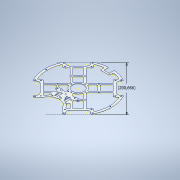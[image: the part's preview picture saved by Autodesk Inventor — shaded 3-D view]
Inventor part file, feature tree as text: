
AUTODESK INVENTOR PART (.ipt)
format: ipt  version: 2020 (Build 240168000, 168)  size: 2,045,440 bytes
history: native  units: mm
features: extrude x15, sketch x12, projected_geometry x10, fillet x2, other x1, chamfer x1
ambient origin geometry x8: Origin, YZ Plane, XZ Plane, XY Plane, X Axis, Y Axis, Z Axis, Center Point
bodies: Body1 (feature_tree)
feature tree (41):
  other  "Твердое тело1"
  extrude  "outer"  TaperAngle=45.0deg  [1 undecoded]
  extrude  "inner"  Depth=7.0mm
  sketch  "Эскиз3"
  extrude  "Выдавливание3"  Depth=20.0mm
  extrude  "Выдавливание4"  Depth=7.0mm
  extrude  "Выдавливание5"  Depth=3.2mm
  sketch  "Эскиз5"
  extrude  "Выдавливание7"  Depth=59.0mm
  extrude  "Выдавливание8"  Depth=83.0mm
  sketch  "Эскиз6"
  extrude  "Выдавливание9"  Depth=69.0mm
  extrude  "Выдавливание10"  Depth=55.0mm
  sketch  "Эскиз7"
  sketch  "Эскиз8"
  sketch  "Эскиз9"
  extrude  "Выдавливание11"  Depth=3.0mm
  extrude  "Выдавливание12"  Depth=8.0mm
  sketch  "Эскиз10"
  extrude  "Выдавливание13"  Depth=5.0mm
  extrude  "Выдавливание14"  Depth=2.0mm
  fillet  "Сопряжение1"  Radius=40.0mm
  chamfer  "Фаска1"  Distance=2.0mm
  sketch  "Эскиз11"
  extrude  "Выдавливание15"  Depth=105.0mm
  fillet  "Сопряжение2"  Radius=2.0mm
  extrude  "Выдавливание16"  Depth=2.0mm TaperAngle=0.0deg
  sketch  "Эскиз1"
  sketch  "Эскиз2"
  projected_geometry  "Спроецированная петля1"
  projected_geometry  "Спроецированная петля2"
  sketch  "Эскиз4"
  projected_geometry  "Спроецированная петля3"
  projected_geometry  "Спроецированная петля4"
  projected_geometry  "Спроецированная петля5"
  projected_geometry  "Спроецированная петля6"
  projected_geometry  "Спроецированная петля7"
  projected_geometry  "Спроецированная петля8"
  projected_geometry  "Спроецированная петля9"
  sketch  "Эскиз12"
  projected_geometry  "Спроецированная петля10"
note: 1 required parameter value undecoded (feature->parameter linkage not recoverable at this tier; creation-order binding heuristic only, values carry confidence <= 0.55)
